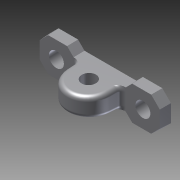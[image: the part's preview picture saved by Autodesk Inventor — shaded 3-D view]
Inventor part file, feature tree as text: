
AUTODESK INVENTOR PART (.ipt)
format: ipt  version: 2014 SP1 (Build 180222100, 222)  size: 391,680 bytes
history: native  units: in
note: dims shown in document units (in); Inventor stores cm internally (conversion verified against a paired STEP export)
features: other x2, imported_body x1, plane x1
ambient origin geometry x8: Origin, YZ Plane, XZ Plane, XY Plane, X Axis, Y Axis, Z Axis, Center Point
bodies: Body1 (feature_tree)
feature tree (4):
  parser-record x1  (decoder bookkeeping rows leaked as tree rows — omitted from the tree; the rows remain in map.json)
  imported_body  "Base1"
  other  "middle"
  plane  "Work Plane1"
